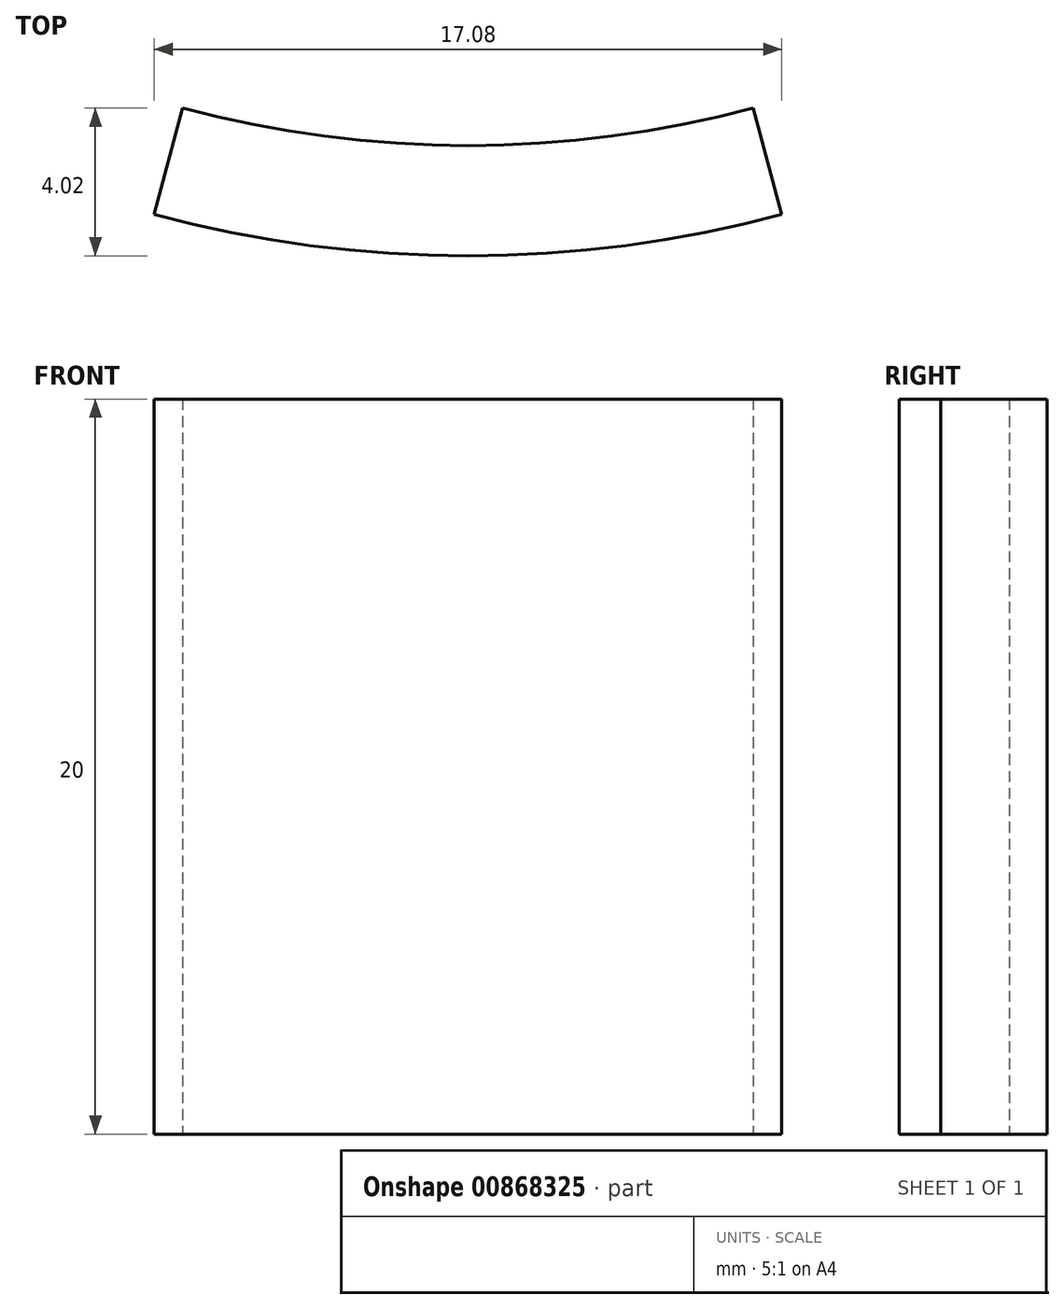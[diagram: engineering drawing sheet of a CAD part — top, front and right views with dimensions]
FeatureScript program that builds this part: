
annotation { "Feature Type Name" : "Feature", "Feature Type Description" : "" }
export const myFeature = defineFeature(function(context is Context, id is Id, definition is map)
    precondition{}
    {
        {
            var Q0;
            Q0=qCreatedBy(makeId("Top.planeOp"),FACE);
            var sketch = newSketch(context, id + "F0", { "sketchPlane" : qUnion([Q0])});
            skLineSegment(sketch, "E0", {"start": v(0, 0) * mm, "end": v(-8.54, -31.88) * mm});
            skLineSegment(sketch, "E1", {"start": v(0, 0) * mm, "end": v(8.54, -31.88) * mm});
            skArc(sketch, "E2", {"start": v(-8.54, -31.88) * mm, "mid": v(0, -33) * mm, "end": v(8.54, -31.88) * mm});
            skArc(sketch, "E3", {"start": v(-7.76, -28.98) * mm, "mid": v(0, -30) * mm, "end": v(7.76, -28.98) * mm});
            skSolve(sketch);
        }
        {
            var Q0;
            {var subQ0=sQuery(id+"F0.wireOp",EDGE,"E2");Q0=makeQuery(id+"F0.imprint","IMPRINT",FACE,{"disambiguationData":[TD([[makeQuery(id+"F0.imprint","IMPRINT",EDGE,{"derivedFrom":subQ0}),1.0]])]});}
            extrude(context, id + "F1", {"entities" : qUnion([Q0]), "endBound" : BoundingType.SYMMETRIC, "depth" : 20 * mm, "offsetDistance" : 25 * mm});
        }
    });
